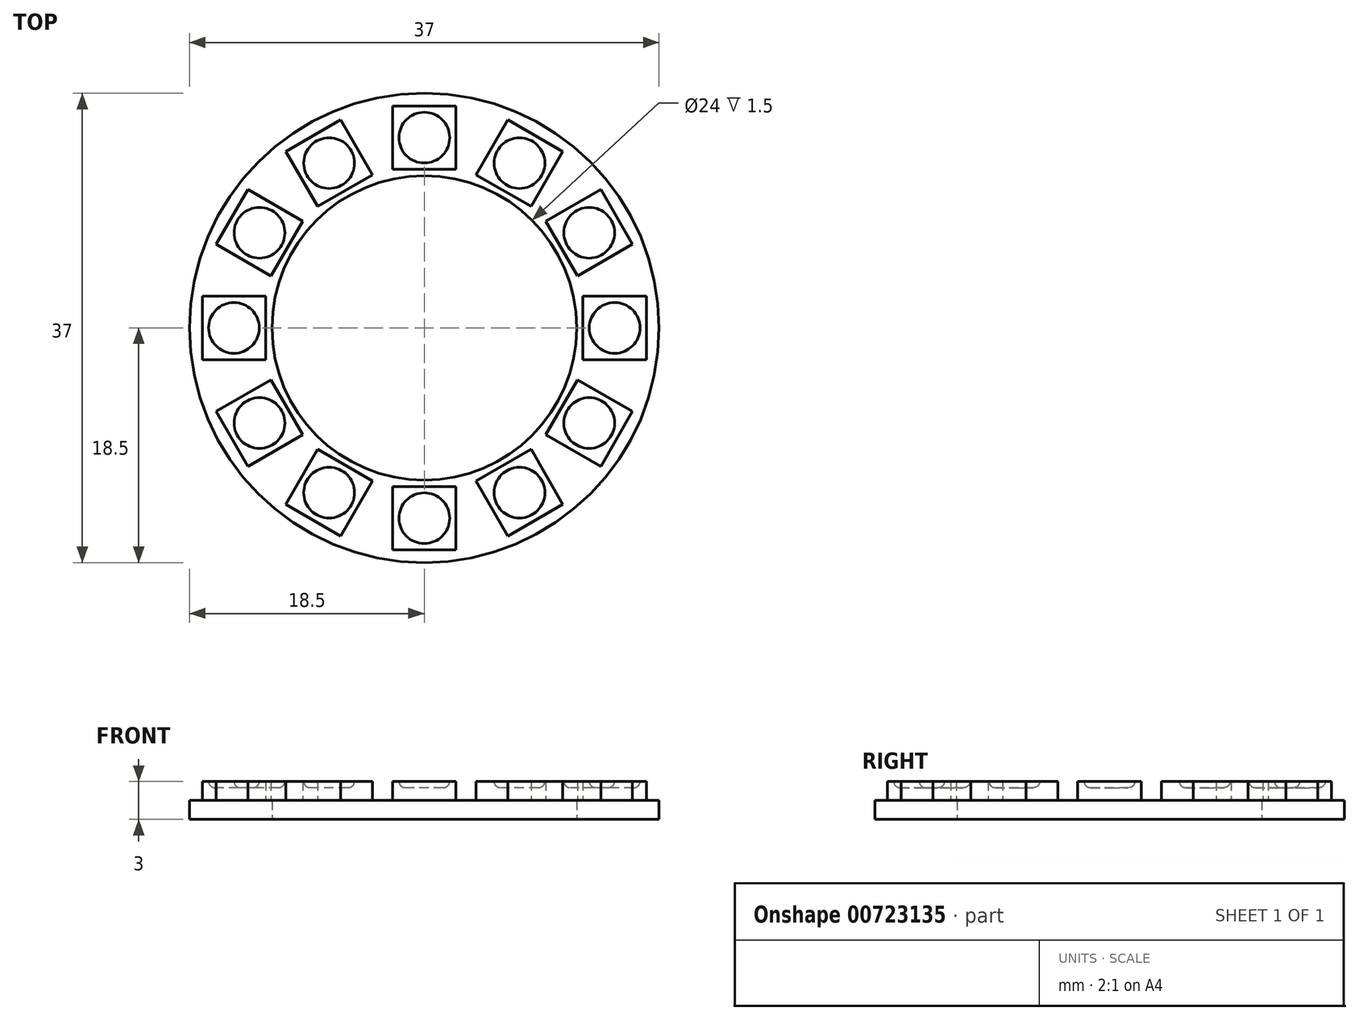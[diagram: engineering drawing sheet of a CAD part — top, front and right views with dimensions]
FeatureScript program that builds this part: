
annotation { "Feature Type Name" : "Feature", "Feature Type Description" : "" }
export const myFeature = defineFeature(function(context is Context, id is Id, definition is map)
    precondition{}
    {
        {
            var Q0;
            Q0=qCreatedBy(makeId("Top.planeOp"),FACE);
            var sketch = newSketch(context, id + "F0", { "sketchPlane" : qUnion([Q0])});
            skCircle(sketch, "E0", {"center": v(0, 0) * mm, "radius": 18.5 * mm});
            skCircle(sketch, "E1", {"center": v(0, 0) * mm, "radius": 12 * mm});
            skSolve(sketch);
        }
        {
            var Q0;
            Q0=makeQuery(id+"F0.imprint","IMPRINT",FACE,{"disambiguationData":[TD([[makeQuery(id+"F0.imprint","IMPRINT",EDGE,{"derivedFrom":sQuery(id+"F0.wireOp",EDGE,"E0")}),1.0]])]});
            var Q1;
            Q1=sQuery(id+"F0.wireOp",EDGE,"E0");
            extrude(context, id + "F1", {"entities" : qUnion([Q0]), "surfaceEntities" : qUnion([Q1]), "depth" : 1.5 * mm, "offsetDistance" : 25 * mm});
        }
        {
            var Q0;
            Q0=makeQuery(id+"F1.opExtrude","CAP_FACE",FACE,{"disambiguationData":[OSD([sQuery(id+"F0.wireOp",EDGE,"E0"),sQuery(id+"F0.wireOp",EDGE,"E1")])],"isStart":false});
            var sketch = newSketch(context, id + "F2", { "sketchPlane" : qUnion([Q0])});
            skLineSegment(sketch, "E2.bottom", {"start": v(-12.5, 2.5) * mm, "end": v(-17.5, 2.5) * mm});
            skLineSegment(sketch, "E2.top", {"start": v(-12.5, -2.5) * mm, "end": v(-17.5, -2.5) * mm});
            skLineSegment(sketch, "E2.left", {"start": v(-12.5, 2.5) * mm, "end": v(-12.5, -2.5) * mm});
            skLineSegment(sketch, "E2.right", {"start": v(-17.5, 2.5) * mm, "end": v(-17.5, -2.5) * mm});
            skPoint(sketch, "E2.middle", {"position": v(-15, 0) * mm});
            skLineSegment(sketch, "E3.1.0", {"start": v(-12.08, -4.08) * mm, "end": v(-9.58, -8.42) * mm});
            skLineSegment(sketch, "E3.1.1", {"start": v(-12.08, -4.08) * mm, "end": v(-16.4, -6.58) * mm});
            skLineSegment(sketch, "E3.1.2", {"start": v(-16.4, -6.58) * mm, "end": v(-13.9, -10.92) * mm});
            skLineSegment(sketch, "E3.1.3", {"start": v(-9.58, -8.42) * mm, "end": v(-13.9, -10.92) * mm});
            skLineSegment(sketch, "E3.2.0", {"start": v(-8.42, -9.58) * mm, "end": v(-4.08, -12.08) * mm});
            skLineSegment(sketch, "E3.2.1", {"start": v(-8.42, -9.58) * mm, "end": v(-10.92, -13.9) * mm});
            skLineSegment(sketch, "E3.2.2", {"start": v(-10.92, -13.9) * mm, "end": v(-6.58, -16.4) * mm});
            skLineSegment(sketch, "E3.2.3", {"start": v(-4.08, -12.08) * mm, "end": v(-6.58, -16.4) * mm});
            skLineSegment(sketch, "E3.3.0", {"start": v(-2.5, -12.5) * mm, "end": v(2.5, -12.5) * mm});
            skLineSegment(sketch, "E3.3.1", {"start": v(-2.5, -12.5) * mm, "end": v(-2.5, -17.5) * mm});
            skLineSegment(sketch, "E3.3.2", {"start": v(-2.5, -17.5) * mm, "end": v(2.5, -17.5) * mm});
            skLineSegment(sketch, "E3.3.3", {"start": v(2.5, -12.5) * mm, "end": v(2.5, -17.5) * mm});
            skLineSegment(sketch, "E3.4.0", {"start": v(4.08, -12.08) * mm, "end": v(8.42, -9.58) * mm});
            skLineSegment(sketch, "E3.4.1", {"start": v(4.08, -12.08) * mm, "end": v(6.58, -16.4) * mm});
            skLineSegment(sketch, "E3.4.2", {"start": v(6.58, -16.4) * mm, "end": v(10.92, -13.9) * mm});
            skLineSegment(sketch, "E3.4.3", {"start": v(8.42, -9.58) * mm, "end": v(10.92, -13.9) * mm});
            skLineSegment(sketch, "E3.5.0", {"start": v(9.58, -8.42) * mm, "end": v(12.08, -4.08) * mm});
            skLineSegment(sketch, "E3.5.1", {"start": v(9.58, -8.42) * mm, "end": v(13.9, -10.92) * mm});
            skLineSegment(sketch, "E3.5.2", {"start": v(13.9, -10.92) * mm, "end": v(16.4, -6.58) * mm});
            skLineSegment(sketch, "E3.5.3", {"start": v(12.08, -4.08) * mm, "end": v(16.4, -6.58) * mm});
            skLineSegment(sketch, "E3.6.0", {"start": v(12.5, -2.5) * mm, "end": v(12.5, 2.5) * mm});
            skLineSegment(sketch, "E3.6.1", {"start": v(12.5, -2.5) * mm, "end": v(17.5, -2.5) * mm});
            skLineSegment(sketch, "E3.6.2", {"start": v(17.5, -2.5) * mm, "end": v(17.5, 2.5) * mm});
            skLineSegment(sketch, "E3.6.3", {"start": v(12.5, 2.5) * mm, "end": v(17.5, 2.5) * mm});
            skLineSegment(sketch, "E3.7.0", {"start": v(12.08, 4.08) * mm, "end": v(9.58, 8.42) * mm});
            skLineSegment(sketch, "E3.7.1", {"start": v(12.08, 4.08) * mm, "end": v(16.4, 6.58) * mm});
            skLineSegment(sketch, "E3.7.2", {"start": v(16.4, 6.58) * mm, "end": v(13.9, 10.92) * mm});
            skLineSegment(sketch, "E3.7.3", {"start": v(9.58, 8.42) * mm, "end": v(13.9, 10.92) * mm});
            skLineSegment(sketch, "E3.8.0", {"start": v(8.42, 9.58) * mm, "end": v(4.08, 12.08) * mm});
            skLineSegment(sketch, "E3.8.1", {"start": v(8.42, 9.58) * mm, "end": v(10.92, 13.9) * mm});
            skLineSegment(sketch, "E3.8.2", {"start": v(10.92, 13.9) * mm, "end": v(6.58, 16.4) * mm});
            skLineSegment(sketch, "E3.8.3", {"start": v(4.08, 12.08) * mm, "end": v(6.58, 16.4) * mm});
            skLineSegment(sketch, "E3.9.0", {"start": v(2.5, 12.5) * mm, "end": v(-2.5, 12.5) * mm});
            skLineSegment(sketch, "E3.9.1", {"start": v(2.5, 12.5) * mm, "end": v(2.5, 17.5) * mm});
            skLineSegment(sketch, "E3.9.2", {"start": v(2.5, 17.5) * mm, "end": v(-2.5, 17.5) * mm});
            skLineSegment(sketch, "E3.9.3", {"start": v(-2.5, 12.5) * mm, "end": v(-2.5, 17.5) * mm});
            skLineSegment(sketch, "E3.10.0", {"start": v(-4.08, 12.08) * mm, "end": v(-8.42, 9.58) * mm});
            skLineSegment(sketch, "E3.10.1", {"start": v(-4.08, 12.08) * mm, "end": v(-6.58, 16.4) * mm});
            skLineSegment(sketch, "E3.10.2", {"start": v(-6.58, 16.4) * mm, "end": v(-10.92, 13.9) * mm});
            skLineSegment(sketch, "E3.10.3", {"start": v(-8.42, 9.58) * mm, "end": v(-10.92, 13.9) * mm});
            skLineSegment(sketch, "E3.11.0", {"start": v(-9.58, 8.42) * mm, "end": v(-12.08, 4.08) * mm});
            skLineSegment(sketch, "E3.11.1", {"start": v(-9.58, 8.42) * mm, "end": v(-13.9, 10.92) * mm});
            skLineSegment(sketch, "E3.11.2", {"start": v(-13.9, 10.92) * mm, "end": v(-16.4, 6.58) * mm});
            skLineSegment(sketch, "E3.11.3", {"start": v(-12.08, 4.08) * mm, "end": v(-16.4, 6.58) * mm});
            skPoint(sketch, "E3.center", {"position": v(0, 0) * mm});
            skSolve(sketch);
        }
        {
            var Q0;
            Q0 = qSketchRegion(id + "F2", true);
            extrude(context, id + "F3", {"entities" : qUnion([Q0]), "depth" : 1.5 * mm, "offsetDistance" : 25 * mm});
        }
        {
            var Q0;
            Q0=makeQuery(id+"F3.opExtrude","CAP_FACE",FACE,{"disambiguationData":[OSD([sQuery(id+"F2.wireOp",EDGE,"E2.bottom"),sQuery(id+"F2.wireOp",EDGE,"E2.top"),sQuery(id+"F2.wireOp",EDGE,"E2.left"),sQuery(id+"F2.wireOp",EDGE,"E2.right")])],"isStart":false});
            var sketch = newSketch(context, id + "F4", { "sketchPlane" : qUnion([Q0])});
            skCircle(sketch, "E4", {"center": v(-15, 0) * mm, "radius": 2 * mm});
            skCircle(sketch, "E5.1.0", {"center": v(-13, -7.5) * mm, "radius": 2 * mm});
            skCircle(sketch, "E5.2.0", {"center": v(-7.5, -13) * mm, "radius": 2 * mm});
            skCircle(sketch, "E5.3.0", {"center": v(0, -15) * mm, "radius": 2 * mm});
            skCircle(sketch, "E5.4.0", {"center": v(7.5, -13) * mm, "radius": 2 * mm});
            skCircle(sketch, "E5.5.0", {"center": v(13, -7.5) * mm, "radius": 2 * mm});
            skCircle(sketch, "E5.6.0", {"center": v(15, 0) * mm, "radius": 2 * mm});
            skCircle(sketch, "E5.7.0", {"center": v(13, 7.5) * mm, "radius": 2 * mm});
            skCircle(sketch, "E5.8.0", {"center": v(7.5, 13) * mm, "radius": 2 * mm});
            skCircle(sketch, "E5.9.0", {"center": v(0, 15) * mm, "radius": 2 * mm});
            skCircle(sketch, "E5.10.0", {"center": v(-7.5, 13) * mm, "radius": 2 * mm});
            skCircle(sketch, "E5.11.0", {"center": v(-13, 7.5) * mm, "radius": 2 * mm});
            skPoint(sketch, "E5.center", {"position": v(0, 0) * mm});
            skSolve(sketch);
        }
        {
            var Q0;
            Q0 = qSketchRegion(id + "F4", true);
            extrude(context, id + "F5", {"entities" : qUnion([Q0]), "operationType" : NewBodyOperationType.REMOVE, "oppositeDirection" : true, "depth" : 0.5 * mm, "offsetDistance" : 25 * mm});
        }
        {
            var Q0;
            Q0=makeQuery(id+"F5.boolean.opBoolean","COPY",FACE,{"derivedFrom":makeQuery(id+"F5.opExtrude","CAP_FACE",FACE,{"disambiguationData":[OSD([sQuery(id+"F4.wireOp",EDGE,"E4")])],"isStart":false})});
            var Q1;
            Q1=makeQuery(id+"F5.boolean.opBoolean","COPY",FACE,{"derivedFrom":makeQuery(id+"F5.opExtrude","CAP_FACE",FACE,{"disambiguationData":[OSD([sQuery(id+"F4.wireOp",EDGE,"E5.11.0")])],"isStart":false})});
            var Q2;
            Q2=makeQuery(id+"F5.boolean.opBoolean","COPY",FACE,{"derivedFrom":makeQuery(id+"F5.opExtrude","CAP_FACE",FACE,{"disambiguationData":[OSD([sQuery(id+"F4.wireOp",EDGE,"E5.10.0")])],"isStart":false})});
            var Q3;
            Q3=makeQuery(id+"F5.boolean.opBoolean","COPY",FACE,{"derivedFrom":makeQuery(id+"F5.opExtrude","CAP_FACE",FACE,{"disambiguationData":[OSD([sQuery(id+"F4.wireOp",EDGE,"E5.9.0")])],"isStart":false})});
            var Q4;
            Q4=makeQuery(id+"F5.boolean.opBoolean","COPY",FACE,{"derivedFrom":makeQuery(id+"F5.opExtrude","CAP_FACE",FACE,{"disambiguationData":[OSD([sQuery(id+"F4.wireOp",EDGE,"E5.8.0")])],"isStart":false})});
            var Q5;
            Q5=makeQuery(id+"F5.boolean.opBoolean","COPY",FACE,{"derivedFrom":makeQuery(id+"F5.opExtrude","CAP_FACE",FACE,{"disambiguationData":[OSD([sQuery(id+"F4.wireOp",EDGE,"E5.7.0")])],"isStart":false})});
            var Q6;
            Q6=makeQuery(id+"F5.boolean.opBoolean","COPY",FACE,{"derivedFrom":makeQuery(id+"F5.opExtrude","CAP_FACE",FACE,{"disambiguationData":[OSD([sQuery(id+"F4.wireOp",EDGE,"E5.6.0")])],"isStart":false})});
            var Q7;
            Q7=makeQuery(id+"F5.boolean.opBoolean","COPY",FACE,{"derivedFrom":makeQuery(id+"F5.opExtrude","CAP_FACE",FACE,{"disambiguationData":[OSD([sQuery(id+"F4.wireOp",EDGE,"E5.5.0")])],"isStart":false})});
            var Q8;
            Q8=makeQuery(id+"F5.boolean.opBoolean","COPY",FACE,{"derivedFrom":makeQuery(id+"F5.opExtrude","CAP_FACE",FACE,{"disambiguationData":[OSD([sQuery(id+"F4.wireOp",EDGE,"E5.4.0")])],"isStart":false})});
            var Q9;
            Q9=makeQuery(id+"F5.boolean.opBoolean","COPY",FACE,{"derivedFrom":makeQuery(id+"F5.opExtrude","CAP_FACE",FACE,{"disambiguationData":[OSD([sQuery(id+"F4.wireOp",EDGE,"E5.3.0")])],"isStart":false})});
            var Q10;
            Q10=makeQuery(id+"F5.boolean.opBoolean","COPY",FACE,{"derivedFrom":makeQuery(id+"F5.opExtrude","CAP_FACE",FACE,{"disambiguationData":[OSD([sQuery(id+"F4.wireOp",EDGE,"E5.2.0")])],"isStart":false})});
            var Q11;
            Q11=makeQuery(id+"F5.boolean.opBoolean","COPY",FACE,{"derivedFrom":makeQuery(id+"F5.opExtrude","CAP_FACE",FACE,{"disambiguationData":[OSD([sQuery(id+"F4.wireOp",EDGE,"E5.1.0")])],"isStart":false})});
            fillet(context, id + "F6", {"entities" : qUnion([Q0, Q1, Q2, Q3, Q4, Q5, Q6, Q7, Q8, Q9, Q10, Q11]), "radius" : 0.5 * mm, "tangentPropagation" : true, "allowEdgeOverflow" : false});
        }
    });
